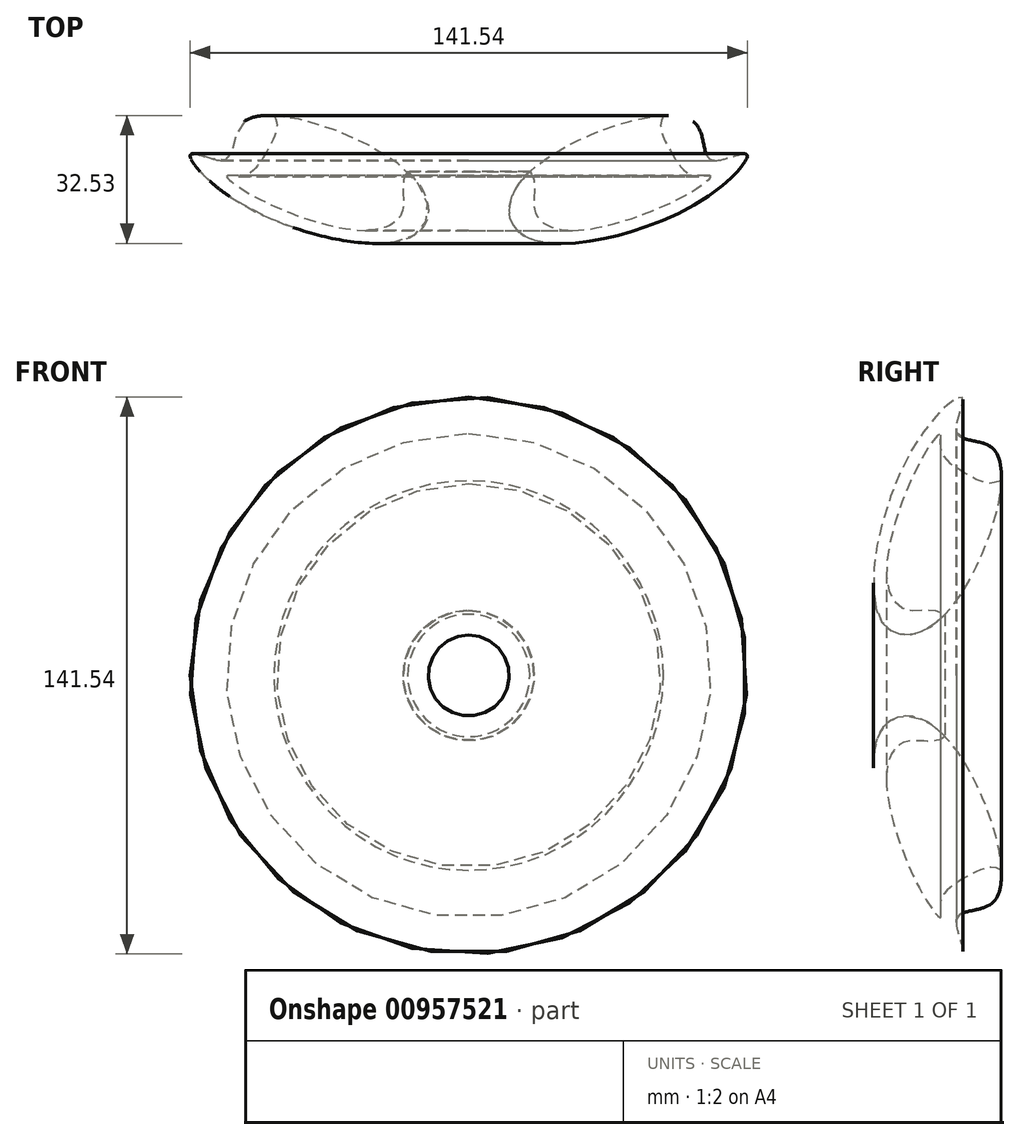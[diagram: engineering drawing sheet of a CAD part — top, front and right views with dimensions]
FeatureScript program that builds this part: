
annotation { "Feature Type Name" : "Feature", "Feature Type Description" : "" }
export const myFeature = defineFeature(function(context is Context, id is Id, definition is map)
    precondition{}
    {
        {
            var Q0;
            Q0=qCreatedBy(makeId("Top.planeOp"),FACE);
            var sketch = newSketch(context, id + "F0", { "sketchPlane" : qUnion([Q0])});
            skFitSpline(sketch, "E0", {"points": [v(-42.83, 29.13) * mm, v(-47.34, 19.46) * mm, v(-56.2, 20.9) * mm, v(-45.24, 9.15) * mm, v(0, 0) * mm, v(0, 14.95) * mm, v(-42.83, 29.13) * mm]});
            skLineSegment(sketch, "E1", {"start": v(14.14, 16.35) * mm, "end": v(14.14, -14.3) * mm});
            skSolve(sketch);
        }
        {
            var Q0;
            Q0=makeQuery(id+"F0.imprint","IMPRINT",FACE,{"disambiguationData":[TD([[makeQuery(id+"F0.imprint","IMPRINT",EDGE,{"derivedFrom":sQuery(id+"F0.wireOp",EDGE,"E0")}),1.0]])]});
            var Q1;
            Q1=sQuery(id+"F0.wireOp",EDGE,"E1");
            revolve(context, id + "F1", {"surfaceOperationType" : NewSurfaceOperationType.NEW, "entities" : qUnion([Q0]), "axis" : qUnion([Q1]), "revolveType" : RevolveType.FULL});
        }
        {
            var Q0;
            Q0=qCreatedBy(makeId("Top.planeOp"),FACE);
            var sketch = newSketch(context, id + "F2", { "sketchPlane" : qUnion([Q0])});
            skFitSpline(sketch, "E2", {"points": [v(-40.42, 36.22) * mm, v(-35.42, 30.74) * mm, v(-36.71, 22.36) * mm, v(-43, 15.27) * mm, v(-47.35, 15.27) * mm, v(-41.87, 10.92) * mm, v(-19.8, 2.38) * mm, v(-7.06, 2.22) * mm, v(-2.7, 6.24) * mm, v(-2.55, 12.85) * mm, v(0, 17.04) * mm, v(3.74, 16.56) * mm, v(-40.42, 36.22) * mm]});
            skSolve(sketch);
        }
        {
            var Q0;
            Q0=makeQuery(id+"F2.imprint","IMPRINT",FACE,{"disambiguationData":[TD([[makeQuery(id+"F2.imprint","IMPRINT",EDGE,{"derivedFrom":sQuery(id+"F2.wireOp",EDGE,"E2")}),1.0]])]});
            var Q1;
            Q1 = qSketchRegion(id + "F0", true);
            var Q2;
            Q2=sQuery(id+"F0.wireOp",EDGE,"E1");
            revolve(context, id + "F3", {"surfaceOperationType" : NewSurfaceOperationType.NEW, "entities" : qUnion([Q0, Q1]), "axis" : qUnion([Q2]), "revolveType" : RevolveType.FULL});
        }
        {
            var Q0;
            Q0=makeQuery(id+"F3.opRevolve","SWEPT_BODY",BODY,{"disambiguationData":[OSD([sQuery(id+"F2.wireOp",EDGE,"E2")])]});
            var Q1;
            Q1=makeQuery(id+"F3.opRevolve","SWEPT_BODY",BODY,{"disambiguationData":[OSD([sQuery(id+"F0.wireOp",EDGE,"E0")])]});
            booleanBodies(context, id + "F4", {"operationType" : BooleanOperationType.SUBTRACTION, "tools" : qUnion([Q0]), "targets" : qUnion([Q1])});
        }
    });
